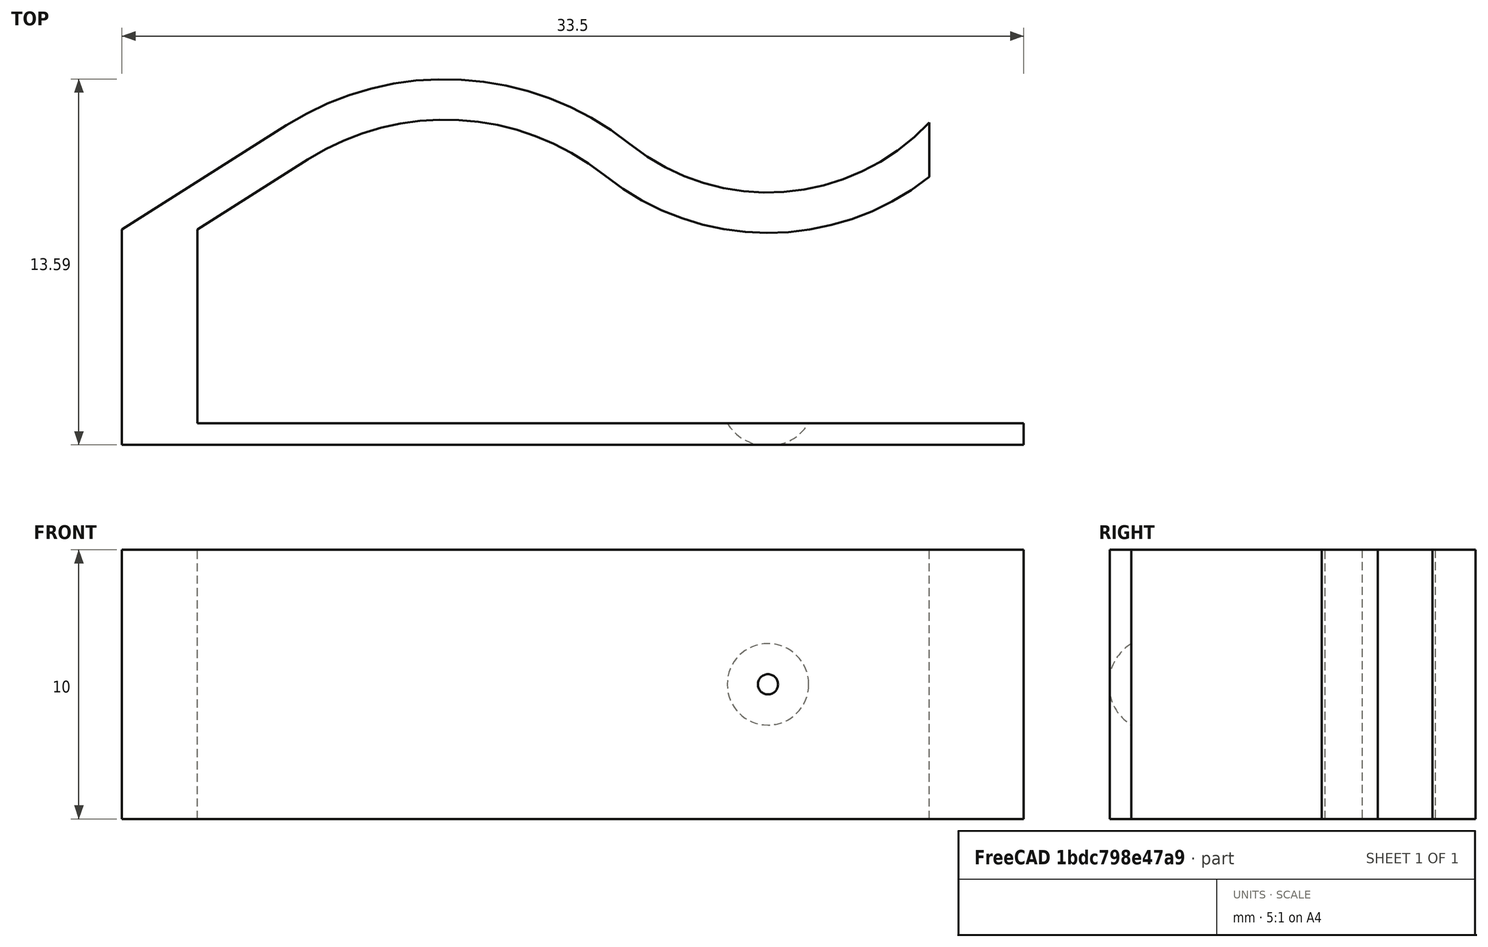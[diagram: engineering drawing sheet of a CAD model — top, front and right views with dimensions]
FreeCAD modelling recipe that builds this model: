
FCSTD DOCUMENT  (FreeCAD 0.16R5342 (Git))
Label: BluRay2LensHolder
License: All rights reserved
LicenseURL: http://en.wikipedia.org/wiki/All_rights_reserved
objects: Sketcher::SketchObject×2, Mesh::Feature×1, App::DocumentObjectGroup×1, PartDesign::Pad×1, Part::Revolution×1, Part::Cut×1
note: 6 computed .brp shape members not serialized (recipe doc carries the construction recipe); baked Part::Feature solids carry a one-line shape summary decoded from their .brp

FEATURE [Mesh::Feature] _50Clip  label="350Clip"
  Placement = pos=(0,-2,0) rot=(0,0,1;0rad)
FEATURE [App::DocumentObjectGroup] Group  label="Reference"
  Group = -> [_50Clip]
FEATURE [Sketcher::SketchObject] Sketch  label="Base"
  sketch-geometry (14):
    g0: LineSegment StartX=0 StartY=8 StartZ=0 EndX=0 EndY=0 EndZ=0
    g1: LineSegment StartX=0 StartY=0 StartZ=0 EndX=33.5 EndY=0 EndZ=0
    g2: LineSegment StartX=33.5 StartY=0 StartZ=0 EndX=33.5 EndY=0.8 EndZ=0
    g3: LineSegment StartX=33.5 StartY=0.8 StartZ=0 EndX=2.8 EndY=0.8 EndZ=0
    g4: LineSegment StartX=2.8 StartY=0.8 StartZ=0 EndX=2.8 EndY=8 EndZ=0
    g5: LineSegment StartX=0 StartY=8 StartZ=0 EndX=6.10713 EndY=11.8746 EndZ=0
    g6: LineSegment StartX=2.8 StartY=8 StartZ=0 EndX=6.91071 EndY=10.608 EndZ=0
    g7: ArcOfCircle CenterX=12 CenterY=2.58618 CenterZ=0 NormalX=0 NormalY=0 NormalZ=1 Radius=11 StartAngle=0.896055 EndAngle=2.13615
    g8: ArcOfCircle CenterX=12 CenterY=2.58618 CenterZ=0 NormalX=0 NormalY=0 NormalZ=1 Radius=9.5 StartAngle=0.896055 EndAngle=2.13615
    g9: ArcOfCircle CenterX=24 CenterY=17.5862 CenterZ=0 NormalX=0 NormalY=0 NormalZ=1 Radius=9.70937 StartAngle=4.03765 EndAngle=5.37853
    g10: ArcOfCircle CenterX=24 CenterY=17.5862 CenterZ=0 NormalX=0 NormalY=0 NormalZ=1 Radius=8.20937 StartAngle=4.03765 EndAngle=5.53199
    g11: LineSegment StartX=30 StartY=11.9832 StartZ=0 EndX=30 EndY=9.95257 EndZ=0
    g12: LineSegment [constr] StartX=6.10713 StartY=11.8746 StartZ=0 EndX=6.91071 EndY=10.608 EndZ=0
    g13: LineSegment [constr] StartX=18.8716 StartY=11.1757 StartZ=0 EndX=17.9346 EndY=10.0044 EndZ=0
  constraints (42):
    c: Coincident(g0,g1)
    c: Coincident(g1,g2)
    c: Coincident(g2,g3)
    c: Coincident(g3,g4)
    c: Coincident(g0,g5)
    c: Coincident(g4,g6)
    c: Coincident(g7,g5)
    c: Coincident(g6,g8)
    c: Coincident(g8,g9)
    c: Coincident(g7,g10)
    c: Coincident(g9,g11)
    c: Coincident(g10,g11)
    c: Horizontal(g3)
    c: Horizontal(g1)
    c: Vertical(g2)
    c: Vertical(g4)
    c: Vertical(g0)
    c: Tangent(g7,g5)
    c: Tangent(g6,g8)
    c: Tangent(g7,g10)
    c: Tangent(g8,g9)
    c: Parallel(g6,g5)
    c: Coincident(g7,g8)
    c: Coincident(g9,g10)
    c: Vertical(g11)
    c: Coincident(g0,g-1)
    c: DistanceY(g2) = 0.8
    c: DistanceX(g1) = 33.5
    c: DistanceX(g0,g4) = 2.8
    c: DistanceY(g0) = 8
    c: DistanceY(g4,g0) = 0
    c: DistanceX(g9) = 30
    c: Coincident(g12,g6)
    c: Coincident(g12,g5)
    c: Coincident(g13,g8)
    c: Coincident(g13,g7)
    c: Equal(g12,g13)
    c: Distance(g12) = 1.5
    c: DistanceX(g7) = 12
    c: DistanceX(g7,g9) = 12
    c: DistanceY(g9,g7) = -15
    c: Radius(g7) = 11
FEATURE [PartDesign::Pad] Pad  label="Base001"
  Length = 10
  Length2 = 100
  Sketch = -> Sketch
  Type = 0
FEATURE [Sketcher::SketchObject] Sketch001  label="Sphere"
  sketch-geometry (3):
    g0: ArcOfCircle CenterX=0 CenterY=-0.741731 CenterZ=0 NormalX=0 NormalY=0 NormalZ=1 Radius=1.78173 StartAngle=1.5708 EndAngle=2.71222
    g1: LineSegment StartX=0 StartY=1.04 StartZ=0 EndX=0 EndY=0 EndZ=0
    g2: LineSegment StartX=0 StartY=0 StartZ=0 EndX=-1.62 EndY=1e-12 EndZ=0
  constraints (10):
    c: PointOnObject(g0,g-1)
    c: PointOnObject(g0,g-2)
    c: Coincident(g2,g0)
    c: Coincident(g2,g-1)
    c: Coincident(g1,g-1)
    c: Coincident(g1,g0)
    c: DistanceY(g1) = -1.04
    c: DistanceX(g2) = -1.62
    c: PointOnObject(g0,g-2)
    c: Radius(g0) = 1.78173
FEATURE [Part::Revolution] Revolve  label="Spherecut"
  Angle = 360
  Axis = (0,1,0)
  Base = (0,0,0)
  Placement = pos=(24,1,5) rot=(0,0,1;3.14159rad)
  Solid = true
  Source = -> Sketch001
FEATURE [Part::Cut] Cut  label="SphereCut"
  Base = -> Pad
  Tool = -> Revolve
